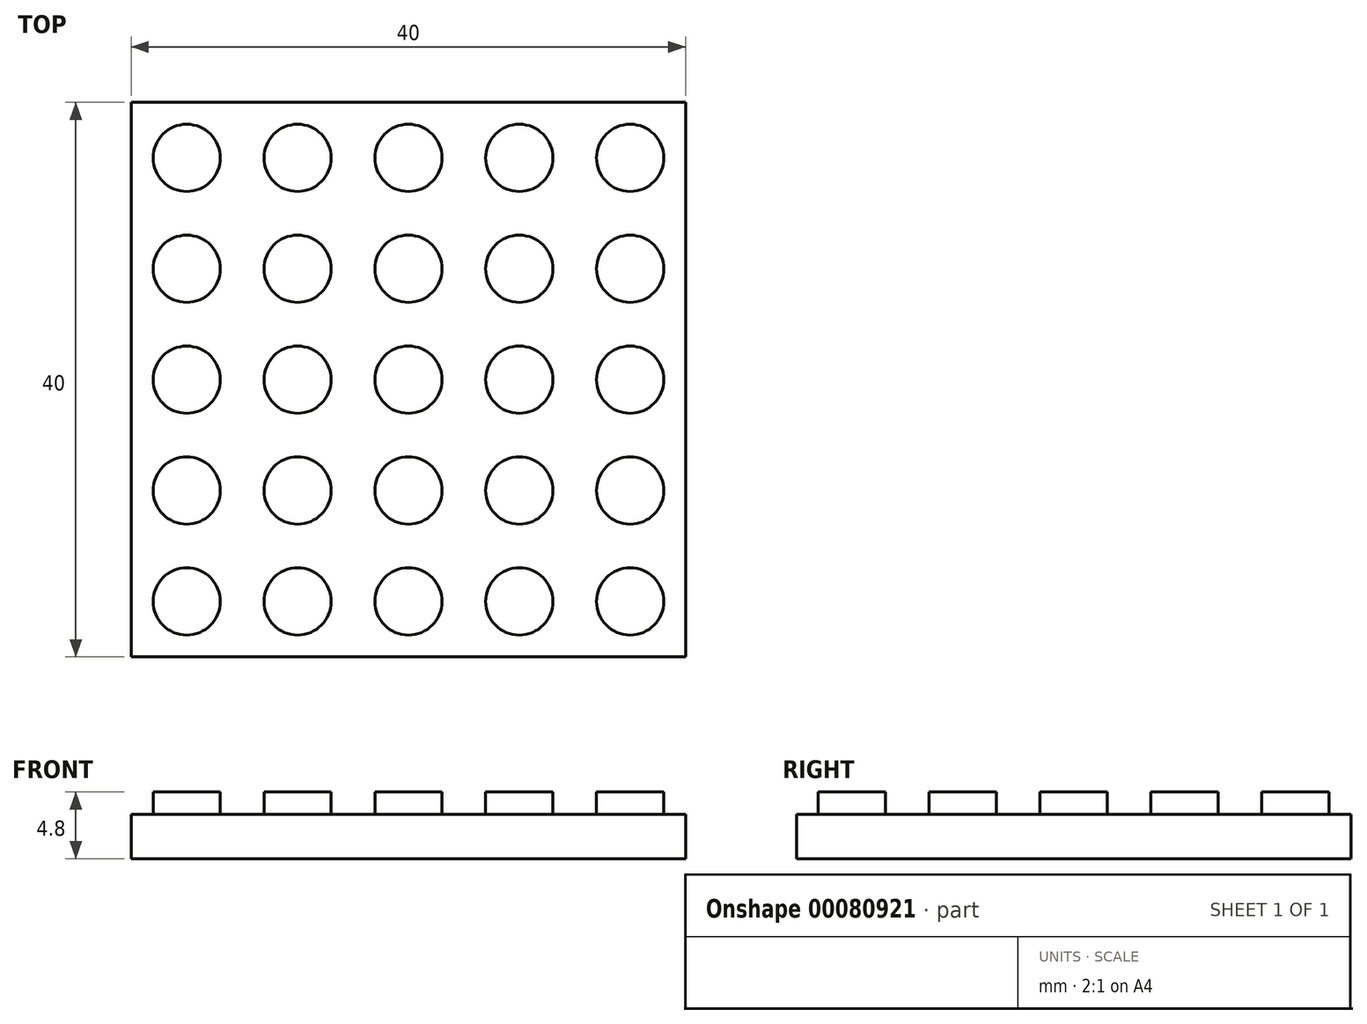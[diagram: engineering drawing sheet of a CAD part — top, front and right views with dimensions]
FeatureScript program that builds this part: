
annotation { "Feature Type Name" : "Feature", "Feature Type Description" : "" }
export const myFeature = defineFeature(function(context is Context, id is Id, definition is map)
    precondition{}
    {
        {
            var Q0;
            Q0=qCreatedBy(makeId("Top.planeOp"),FACE);
            var sketch = newSketch(context, id + "F0", { "sketchPlane" : qUnion([Q0])});
            skLineSegment(sketch, "E0.bottom", {"start": v(20, -20) * mm, "end": v(-20, -20) * mm});
            skLineSegment(sketch, "E0.top", {"start": v(20, 20) * mm, "end": v(-20, 20) * mm});
            skLineSegment(sketch, "E0.left", {"start": v(20, -20) * mm, "end": v(20, 20) * mm});
            skLineSegment(sketch, "E0.right", {"start": v(-20, -20) * mm, "end": v(-20, 20) * mm});
            skPoint(sketch, "E0.middle", {"position": v(0, 0) * mm});
            skSolve(sketch);
        }
        {
            var Q0;
            Q0 = qSketchRegion(id + "F0", true);
            extrude(context, id + "F1", {"entities" : qUnion([Q0]), "depth" : 3.2 * mm});
        }
        {
            var Q0;
            Q0=makeQuery(id+"F1.opExtrude","CAP_FACE",FACE,{"disambiguationData":[OSD([sQuery(id+"F0.wireOp",EDGE,"E0.bottom"),sQuery(id+"F0.wireOp",EDGE,"E0.top"),sQuery(id+"F0.wireOp",EDGE,"E0.left"),sQuery(id+"F0.wireOp",EDGE,"E0.right")])],"isStart":false});
            var sketch = newSketch(context, id + "F2", { "sketchPlane" : qUnion([Q0])});
            skCircle(sketch, "E1", {"center": v(-16, -16) * mm, "radius": 2.43 * mm});
            skCircle(sketch, "E2.0.1.0", {"center": v(-16, -8) * mm, "radius": 2.43 * mm});
            skCircle(sketch, "E2.0.2.0", {"center": v(-16, 0) * mm, "radius": 2.43 * mm});
            skCircle(sketch, "E2.0.3.0", {"center": v(-16, 8) * mm, "radius": 2.43 * mm});
            skCircle(sketch, "E2.0.4.0", {"center": v(-16, 16) * mm, "radius": 2.43 * mm});
            skCircle(sketch, "E2.1.0.0", {"center": v(-8, -16) * mm, "radius": 2.43 * mm});
            skCircle(sketch, "E2.1.1.0", {"center": v(-8, -8) * mm, "radius": 2.43 * mm});
            skCircle(sketch, "E2.1.2.0", {"center": v(-8, 0) * mm, "radius": 2.43 * mm});
            skCircle(sketch, "E2.1.3.0", {"center": v(-8, 8) * mm, "radius": 2.43 * mm});
            skCircle(sketch, "E2.1.4.0", {"center": v(-8, 16) * mm, "radius": 2.43 * mm});
            skCircle(sketch, "E2.2.0.0", {"center": v(0, -16) * mm, "radius": 2.43 * mm});
            skCircle(sketch, "E2.2.1.0", {"center": v(0, -8) * mm, "radius": 2.43 * mm});
            skCircle(sketch, "E2.2.2.0", {"center": v(0, 0) * mm, "radius": 2.43 * mm});
            skCircle(sketch, "E2.2.3.0", {"center": v(0, 8) * mm, "radius": 2.43 * mm});
            skCircle(sketch, "E2.2.4.0", {"center": v(0, 16) * mm, "radius": 2.43 * mm});
            skCircle(sketch, "E2.3.0.0", {"center": v(8, -16) * mm, "radius": 2.43 * mm});
            skCircle(sketch, "E2.3.1.0", {"center": v(8, -8) * mm, "radius": 2.43 * mm});
            skCircle(sketch, "E2.3.2.0", {"center": v(8, 0) * mm, "radius": 2.43 * mm});
            skCircle(sketch, "E2.3.3.0", {"center": v(8, 8) * mm, "radius": 2.43 * mm});
            skCircle(sketch, "E2.3.4.0", {"center": v(8, 16) * mm, "radius": 2.43 * mm});
            skCircle(sketch, "E2.4.0.0", {"center": v(16, -16) * mm, "radius": 2.43 * mm});
            skCircle(sketch, "E2.4.1.0", {"center": v(16, -8) * mm, "radius": 2.43 * mm});
            skCircle(sketch, "E2.4.2.0", {"center": v(16, 0) * mm, "radius": 2.43 * mm});
            skCircle(sketch, "E2.4.3.0", {"center": v(16, 8) * mm, "radius": 2.43 * mm});
            skCircle(sketch, "E2.4.4.0", {"center": v(16, 16) * mm, "radius": 2.43 * mm});
            skLineSegment(sketch, "E2.direction1", {"start": v(-16, -16) * mm, "end": v(-8, -16) * mm, "construction": true});
            skLineSegment(sketch, "E2.direction2", {"start": v(-16, -16) * mm, "end": v(-16, -8) * mm, "construction": true});
            skSolve(sketch);
        }
        {
            var Q0;
            Q0 = qSketchRegion(id + "F2", true);
            extrude(context, id + "F3", {"entities" : qUnion([Q0]), "operationType" : NewBodyOperationType.ADD, "depth" : 1.6 * mm});
        }
    });
